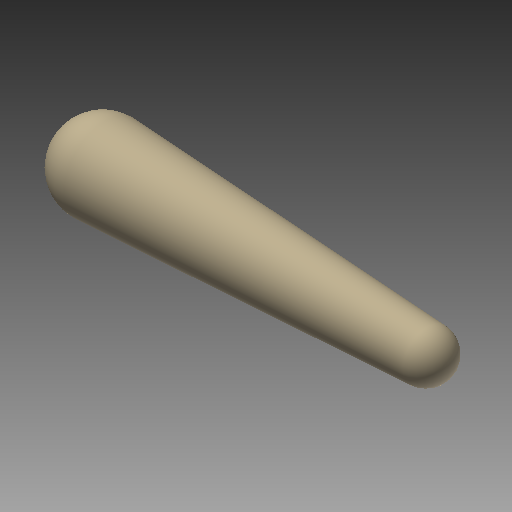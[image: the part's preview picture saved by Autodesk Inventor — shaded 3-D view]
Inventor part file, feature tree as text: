
AUTODESK INVENTOR PART (.ipt)
format: ipt  version: 2022 (Build 260153000, 153)  size: 166,400 bytes
history: native  units: mm (DEFAULTED — no unit token found)
features: other x1, revolve x1, sketch x1
ambient origin geometry x8: Origin, YZ Plane, XZ Plane, XY Plane, X Axis, Y Axis, Z Axis, Center Point
bodies: Solid1 (feature_tree)
feature tree (3):
  other  "iMan - 2D BODY"
  revolve  "Revolution1"  [1 undecoded]
  sketch  "Sketch1"  dims[d1=10.0mm d16=260.096mm d17=122.936mm d18=73.152mm d19=90.0deg d20=519.176mm]
note: 1 required parameter value undecoded (feature->parameter linkage not recoverable at this tier; creation-order binding heuristic only, values carry confidence <= 0.55)
